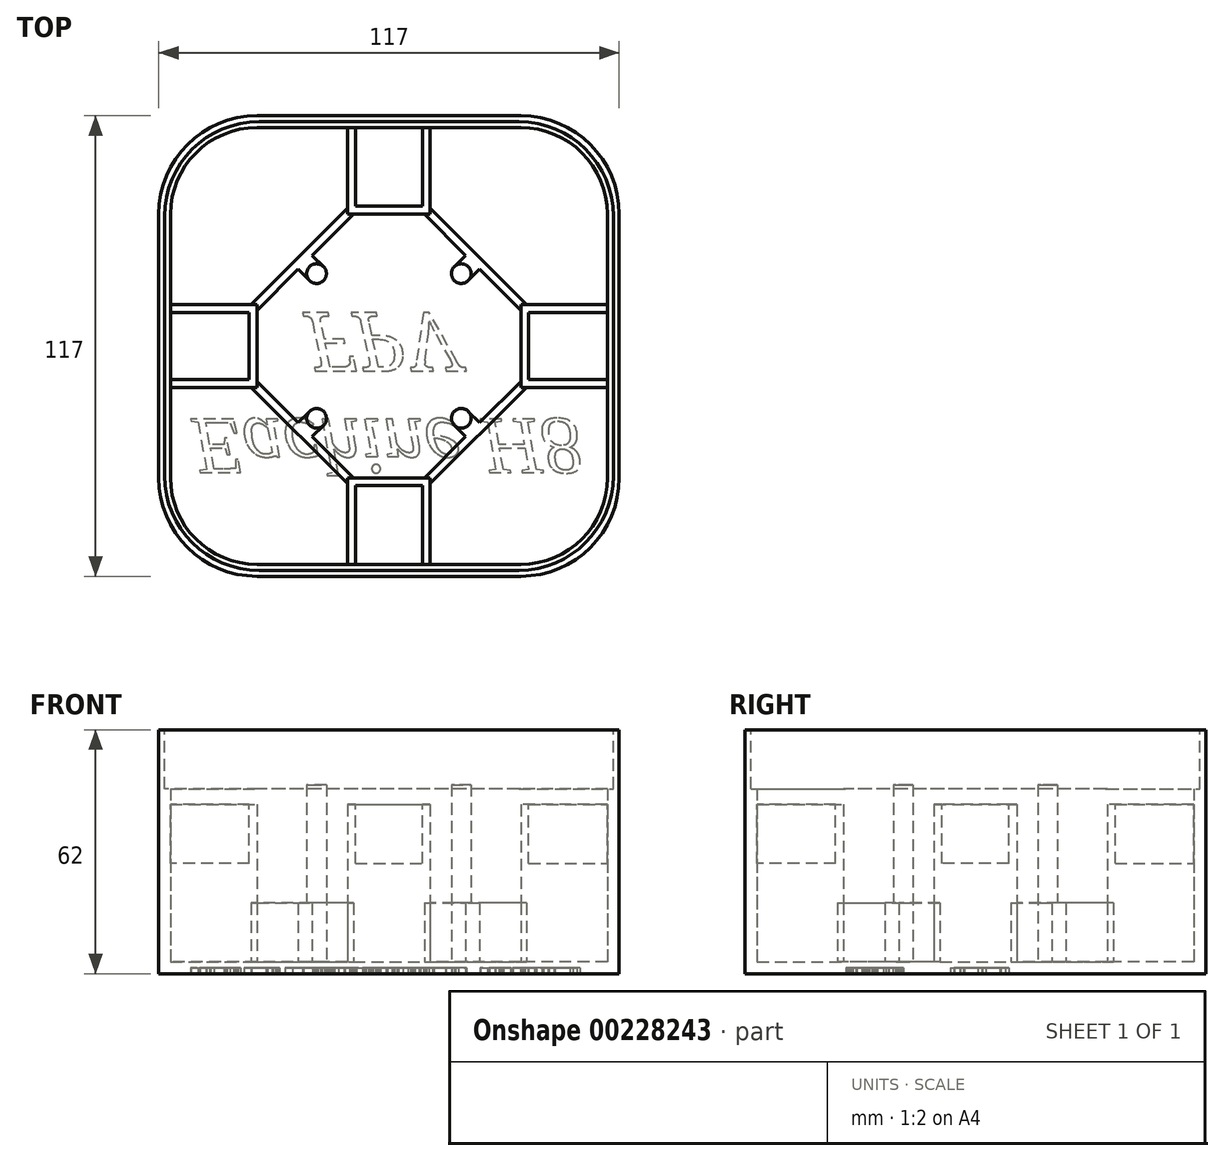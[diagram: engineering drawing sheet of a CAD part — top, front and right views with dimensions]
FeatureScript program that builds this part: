
annotation { "Feature Type Name" : "Feature", "Feature Type Description" : "" }
export const myFeature = defineFeature(function(context is Context, id is Id, definition is map)
    precondition{}
    {
        {
            var Q0;
            Q0=qCreatedBy(makeId("Top.planeOp"),FACE);
            var sketch = newSketch(context, id + "F0", { "sketchPlane" : qUnion([Q0])});
            skLineSegment(sketch, "E0.bottom", {"start": v(33.5, 58.5) * mm, "end": v(-33.5, 58.5) * mm});
            skLineSegment(sketch, "E0.top", {"start": v(33.5, -58.5) * mm, "end": v(-33.5, -58.5) * mm});
            skLineSegment(sketch, "E0.left", {"start": v(58.5, 33.5) * mm, "end": v(58.5, -33.5) * mm});
            skLineSegment(sketch, "E0.right", {"start": v(-58.5, 33.5) * mm, "end": v(-58.5, -33.5) * mm});
            skPoint(sketch, "E0.middle", {"position": v(0, 0) * mm});
            skPoint(sketch, "E1.visualSharp", {"position": v(-58.5, -58.5) * mm});
            skArc(sketch, "E1.filletArc", {"start": v(-58.5, -33.5) * mm, "mid": v(-51.18, -51.18) * mm, "end": v(-33.5, -58.5) * mm});
            skPoint(sketch, "E2.visualSharp", {"position": v(-58.5, 58.5) * mm});
            skArc(sketch, "E2.filletArc", {"start": v(-33.5, 58.5) * mm, "mid": v(-51.18, 51.18) * mm, "end": v(-58.5, 33.5) * mm});
            skPoint(sketch, "E3.visualSharp", {"position": v(58.5, 58.5) * mm});
            skArc(sketch, "E3.filletArc", {"start": v(58.5, 33.5) * mm, "mid": v(51.18, 51.18) * mm, "end": v(33.5, 58.5) * mm});
            skPoint(sketch, "E4.visualSharp", {"position": v(58.5, -58.5) * mm});
            skArc(sketch, "E4.filletArc", {"start": v(33.5, -58.5) * mm, "mid": v(51.18, -51.18) * mm, "end": v(58.5, -33.5) * mm});
            skSolve(sketch);
        }
        {
            var Q0;
            Q0=qSketchRegion(id+"F0",true);
            extrude(context, id + "F1", {"entities" : qUnion([Q0]), "depth" : 62 * mm});
        }
        {
            var Q0;
            Q0=makeQuery(id+"F1.opExtrude","CAP_FACE",FACE,{"disambiguationData":[OSD([sQuery(id+"F0.wireOp",EDGE,"E0.bottom"),sQuery(id+"F0.wireOp",EDGE,"E0.top"),sQuery(id+"F0.wireOp",EDGE,"E0.left"),sQuery(id+"F0.wireOp",EDGE,"E0.right")])],"isStart":false});
            shell(context, id + "F2", {"entities" : qUnion([Q0]), "thickness" : 3 * mm});
        }
        {
            var Q0;
            Q0=makeQuery(id+"F1.opExtrude","CAP_FACE",FACE,{"disambiguationData":[OSD([sQuery(id+"F0.wireOp",EDGE,"E0.bottom"),sQuery(id+"F0.wireOp",EDGE,"E0.top"),sQuery(id+"F0.wireOp",EDGE,"E0.left"),sQuery(id+"F0.wireOp",EDGE,"E0.right")])],"isStart":false});
            var sketch = newSketch(context, id + "F3", { "sketchPlane" : qUnion([Q0])});
            skLineSegment(sketch, "E5.bottom", {"start": v(33, 57) * mm, "end": v(-33, 57) * mm});
            skLineSegment(sketch, "E5.top", {"start": v(33, -57) * mm, "end": v(-33, -57) * mm});
            skLineSegment(sketch, "E5.left", {"start": v(57, 33) * mm, "end": v(57, -33) * mm});
            skLineSegment(sketch, "E5.right", {"start": v(-57, 33) * mm, "end": v(-57, -33) * mm});
            skPoint(sketch, "E5.middle", {"position": v(0, 0) * mm});
            skLineSegment(sketch, "E6.bottom", {"start": v(33.5, 55.5) * mm, "end": v(-33.5, 55.5) * mm});
            skLineSegment(sketch, "E6.top", {"start": v(33.5, -55.5) * mm, "end": v(-33.5, -55.5) * mm});
            skLineSegment(sketch, "E6.left", {"start": v(33.5, 55.5) * mm, "end": v(33.5, -55.5) * mm});
            skLineSegment(sketch, "E6.right", {"start": v(-33.5, 55.5) * mm, "end": v(-33.5, -55.5) * mm});
            skPoint(sketch, "E7.visualSharp", {"position": v(-57, -57) * mm});
            skArc(sketch, "E7.filletArc", {"start": v(-57, -33) * mm, "mid": v(-49.97, -49.97) * mm, "end": v(-33, -57) * mm});
            skPoint(sketch, "E8.visualSharp", {"position": v(57, -57) * mm});
            skArc(sketch, "E8.filletArc", {"start": v(33, -57) * mm, "mid": v(49.97, -49.97) * mm, "end": v(57, -33) * mm});
            skPoint(sketch, "E9.visualSharp", {"position": v(57, 57) * mm});
            skArc(sketch, "E9.filletArc", {"start": v(57, 33) * mm, "mid": v(49.97, 49.97) * mm, "end": v(33, 57) * mm});
            skPoint(sketch, "E10.visualSharp", {"position": v(-57, 57) * mm});
            skArc(sketch, "E10.filletArc", {"start": v(-33, 57) * mm, "mid": v(-49.97, 49.97) * mm, "end": v(-57, 33) * mm});
            skSolve(sketch);
        }
        {
            var Q0;
            Q0=qSketchRegion(id+"F3",true);
            extrude(context, id + "F4", {"entities" : qUnion([Q0]), "operationType" : NewBodyOperationType.REMOVE, "oppositeDirection" : true, "depth" : 15 * mm});
        }
        {
            var Q0;
            Q0=makeQuery(id+"F1.opExtrude","CAP_FACE",FACE,{"disambiguationData":[OSD([sQuery(id+"F0.wireOp",EDGE,"E0.bottom"),sQuery(id+"F0.wireOp",EDGE,"E0.top"),sQuery(id+"F0.wireOp",EDGE,"E0.left"),sQuery(id+"F0.wireOp",EDGE,"E0.right"),sQuery(id+"F0.wireOp",EDGE,"E1.filletArc"),sQuery(id+"F0.wireOp",EDGE,"E2.filletArc"),sQuery(id+"F0.wireOp",EDGE,"E3.filletArc"),sQuery(id+"F0.wireOp",EDGE,"E4.filletArc")])],"isStart":true});
            var sketch = newSketch(context, id + "F5", { "sketchPlane" : qUnion([Q0])});
            skText(sketch, "E11", { "text": "Eachine H8", "fontName": "Tinos-Italic.ttf"});
            skText(sketch, "E12", { "text": "FPV", "fontName": "NotoSerif-Italic.ttf"});
            const initialGuessF5  = {"E11": [-0.05012, 0.0185, 1, 0, 0.015], "E12": [-0.02148, -0.0085, 1, 0, 0.015]};
            skSetInitialGuess(sketch, initialGuessF5);
            skSolve(sketch);
        }
        {
            var Q0;
            Q0=qSketchRegion(id+"F5",true);
            extrude(context, id + "F6", {"entities" : qUnion([Q0]), "operationType" : NewBodyOperationType.REMOVE, "oppositeDirection" : true, "depth" : 1.5 * mm});
        }
        {
            var Q0;
            Q0=makeQuery(id+"F2.opShell","OFFSET_FACE",FACE,{"disambiguationData":[OSD([sQuery(id+"F0.wireOp",EDGE,"E0.bottom"),sQuery(id+"F0.wireOp",EDGE,"E0.top"),sQuery(id+"F0.wireOp",EDGE,"E0.left"),sQuery(id+"F0.wireOp",EDGE,"E0.right"),sQuery(id+"F0.wireOp",EDGE,"E1.filletArc"),sQuery(id+"F0.wireOp",EDGE,"E2.filletArc"),sQuery(id+"F0.wireOp",EDGE,"E3.filletArc"),sQuery(id+"F0.wireOp",EDGE,"E4.filletArc")])]});
            var sketch = newSketch(context, id + "F7", { "sketchPlane" : qUnion([Q0])});
            skLineSegment(sketch, "E13", {"start": v(-18.38, 18.38) * mm, "end": v(18.38, -18.38) * mm, "construction": true});
            skLineSegment(sketch, "E14", {"start": v(-18.38, -18.38) * mm, "end": v(18.38, 18.38) * mm, "construction": true});
            skLineSegment(sketch, "E15.bottom", {"start": v(-18.38, -18.38) * mm, "end": v(18.38, -18.38) * mm, "construction": true});
            skLineSegment(sketch, "E15.top", {"start": v(-18.38, 18.38) * mm, "end": v(18.38, 18.38) * mm, "construction": true});
            skLineSegment(sketch, "E15.left", {"start": v(-18.38, -18.38) * mm, "end": v(-18.38, 18.38) * mm, "construction": true});
            skLineSegment(sketch, "E15.right", {"start": v(18.38, -18.38) * mm, "end": v(18.38, 18.38) * mm, "construction": true});
            skCircle(sketch, "E16", {"center": v(-18.38, 18.38) * mm, "radius": 2.5 * mm});
            skCircle(sketch, "E17", {"center": v(18.38, 18.38) * mm, "radius": 2.5 * mm});
            skCircle(sketch, "E18", {"center": v(18.38, -18.38) * mm, "radius": 2.5 * mm});
            skCircle(sketch, "E19", {"center": v(-18.38, -18.38) * mm, "radius": 2.5 * mm});
            skSolve(sketch);
        }
        {
            var Q0;
            Q0 = qSketchRegion(id + "F7", true);
            extrude(context, id + "F8", {"entities" : qUnion([Q0]), "operationType" : NewBodyOperationType.ADD, "depth" : 45 * mm});
        }
        {
            var Q0;
            Q0=makeQuery(id+"F2.opShell","OFFSET_FACE",FACE,{"disambiguationData":[OSD([sQuery(id+"F0.wireOp",EDGE,"E0.bottom"),sQuery(id+"F0.wireOp",EDGE,"E0.top"),sQuery(id+"F0.wireOp",EDGE,"E0.left"),sQuery(id+"F0.wireOp",EDGE,"E0.right"),sQuery(id+"F0.wireOp",EDGE,"E1.filletArc"),sQuery(id+"F0.wireOp",EDGE,"E2.filletArc"),sQuery(id+"F0.wireOp",EDGE,"E3.filletArc"),sQuery(id+"F0.wireOp",EDGE,"E4.filletArc")])]});
            var sketch = newSketch(context, id + "F9", { "sketchPlane" : qUnion([Q0])});
            skLineSegment(sketch, "E20.bottom", {"start": v(-10.5, 55.5) * mm, "end": v(10.5, 55.5) * mm});
            skLineSegment(sketch, "E20.top", {"start": v(-10.5, 33.5) * mm, "end": v(10.5, 33.5) * mm});
            skLineSegment(sketch, "E20.left", {"start": v(-10.5, 55.5) * mm, "end": v(-10.5, 33.5) * mm});
            skLineSegment(sketch, "E20.right", {"start": v(10.5, 55.5) * mm, "end": v(10.5, 33.5) * mm});
            skLineSegment(sketch, "E21.bottom", {"start": v(55.5, -10.5) * mm, "end": v(33.5, -10.5) * mm});
            skLineSegment(sketch, "E21.top", {"start": v(55.5, 10.5) * mm, "end": v(33.5, 10.5) * mm});
            skLineSegment(sketch, "E21.left", {"start": v(55.5, -10.5) * mm, "end": v(55.5, 10.5) * mm});
            skLineSegment(sketch, "E21.right", {"start": v(33.5, -10.5) * mm, "end": v(33.5, 10.5) * mm});
            skLineSegment(sketch, "E22.bottom", {"start": v(-10.5, -55.5) * mm, "end": v(10.5, -55.5) * mm});
            skLineSegment(sketch, "E22.top", {"start": v(-10.5, -33.5) * mm, "end": v(10.5, -33.5) * mm});
            skLineSegment(sketch, "E22.left", {"start": v(-10.5, -55.5) * mm, "end": v(-10.5, -33.5) * mm});
            skLineSegment(sketch, "E22.right", {"start": v(10.5, -55.5) * mm, "end": v(10.5, -33.5) * mm});
            skLineSegment(sketch, "E23.bottom", {"start": v(-55.5, -10.5) * mm, "end": v(-33.5, -10.5) * mm});
            skLineSegment(sketch, "E23.top", {"start": v(-55.5, 10.5) * mm, "end": v(-33.5, 10.5) * mm});
            skLineSegment(sketch, "E23.left", {"start": v(-55.5, -10.5) * mm, "end": v(-55.5, 10.5) * mm});
            skLineSegment(sketch, "E23.right", {"start": v(-33.5, -10.5) * mm, "end": v(-33.5, 10.5) * mm});
            skSolve(sketch);
        }
        {
            var Q0;
            Q0 = qSketchRegion(id + "F9", true);
            extrude(context, id + "F10", {"entities" : qUnion([Q0]), "operationType" : NewBodyOperationType.ADD, "depth" : 40 * mm});
        }
        {
            var Q0;
            Q0=makeQuery(id+"F10.opExtrude","CAP_FACE",FACE,{"disambiguationData":[OSD([sQuery(id+"F9.wireOp",EDGE,"E23.bottom"),sQuery(id+"F9.wireOp",EDGE,"E23.top"),sQuery(id+"F9.wireOp",EDGE,"E23.left"),sQuery(id+"F9.wireOp",EDGE,"E23.right")])],"isStart":false});
            var sketch = newSketch(context, id + "F11", { "sketchPlane" : qUnion([Q0])});
            skLineSegment(sketch, "E24.bottom", {"start": v(-35.5, 8.5) * mm, "end": v(-55.5, 8.5) * mm});
            skLineSegment(sketch, "E24.top", {"start": v(-35.5, -8.5) * mm, "end": v(-55.5, -8.5) * mm});
            skLineSegment(sketch, "E24.left", {"start": v(-35.5, 8.5) * mm, "end": v(-35.5, -8.5) * mm});
            skLineSegment(sketch, "E24.right", {"start": v(-55.5, 8.5) * mm, "end": v(-55.5, -8.5) * mm});
            skLineSegment(sketch, "E25.bottom", {"start": v(-8.5, 35.5) * mm, "end": v(8.5, 35.5) * mm});
            skLineSegment(sketch, "E25.top", {"start": v(-8.5, 55.5) * mm, "end": v(8.5, 55.5) * mm});
            skLineSegment(sketch, "E25.left", {"start": v(-8.5, 35.5) * mm, "end": v(-8.5, 55.5) * mm});
            skLineSegment(sketch, "E25.right", {"start": v(8.5, 35.5) * mm, "end": v(8.5, 55.5) * mm});
            skLineSegment(sketch, "E26.bottom", {"start": v(35.5, 8.5) * mm, "end": v(55.5, 8.5) * mm});
            skLineSegment(sketch, "E26.top", {"start": v(35.5, -8.5) * mm, "end": v(55.5, -8.5) * mm});
            skLineSegment(sketch, "E26.left", {"start": v(35.5, 8.5) * mm, "end": v(35.5, -8.5) * mm});
            skLineSegment(sketch, "E26.right", {"start": v(55.5, 8.5) * mm, "end": v(55.5, -8.5) * mm});
            skLineSegment(sketch, "E27.bottom", {"start": v(-8.5, -35.5) * mm, "end": v(8.5, -35.5) * mm});
            skLineSegment(sketch, "E27.top", {"start": v(-8.5, -55.5) * mm, "end": v(8.5, -55.5) * mm});
            skLineSegment(sketch, "E27.left", {"start": v(-8.5, -35.5) * mm, "end": v(-8.5, -55.5) * mm});
            skLineSegment(sketch, "E27.right", {"start": v(8.5, -35.5) * mm, "end": v(8.5, -55.5) * mm});
            skSolve(sketch);
        }
        {
            var Q0;
            Q0 = qSketchRegion(id + "F11", true);
            extrude(context, id + "F12", {"entities" : qUnion([Q0]), "operationType" : NewBodyOperationType.REMOVE, "oppositeDirection" : true, "depth" : 15 * mm});
        }
        {
            var Q0;
            Q0=makeQuery(id+"F2.opShell","OFFSET_FACE",FACE,{"disambiguationData":[OSD([sQuery(id+"F0.wireOp",EDGE,"E0.bottom"),sQuery(id+"F0.wireOp",EDGE,"E0.top"),sQuery(id+"F0.wireOp",EDGE,"E0.left"),sQuery(id+"F0.wireOp",EDGE,"E0.right"),sQuery(id+"F0.wireOp",EDGE,"E1.filletArc"),sQuery(id+"F0.wireOp",EDGE,"E2.filletArc"),sQuery(id+"F0.wireOp",EDGE,"E3.filletArc"),sQuery(id+"F0.wireOp",EDGE,"E4.filletArc")])]});
            var sketch = newSketch(context, id + "F13", { "sketchPlane" : qUnion([Q0])});
            skLineSegment(sketch, "E28", {"start": v(-33.5, -10.5) * mm, "end": v(-33.5, -9) * mm});
            skLineSegment(sketch, "E29", {"start": v(-33.5, -9) * mm, "end": v(-9, -33.5) * mm});
            skLineSegment(sketch, "E30", {"start": v(-9, -33.5) * mm, "end": v(-10.5, -33.5) * mm});
            skLineSegment(sketch, "E31", {"start": v(-10.5, -33.5) * mm, "end": v(-10.5, -35) * mm});
            skLineSegment(sketch, "E32", {"start": v(-10.5, -35) * mm, "end": v(-35, -10.5) * mm});
            skLineSegment(sketch, "E33", {"start": v(-35, -10.5) * mm, "end": v(-33.5, -10.5) * mm});
            skLineSegment(sketch, "E34", {"start": v(10.5, -33.5) * mm, "end": v(9, -33.5) * mm});
            skLineSegment(sketch, "E35", {"start": v(9, -33.5) * mm, "end": v(33.5, -9) * mm});
            skLineSegment(sketch, "E36", {"start": v(33.5, -9) * mm, "end": v(33.5, -10.5) * mm});
            skLineSegment(sketch, "E37", {"start": v(33.5, -10.5) * mm, "end": v(35, -10.5) * mm});
            skLineSegment(sketch, "E38", {"start": v(35, -10.5) * mm, "end": v(10.5, -35) * mm});
            skLineSegment(sketch, "E39", {"start": v(10.5, -35) * mm, "end": v(10.5, -33.5) * mm});
            skLineSegment(sketch, "E40", {"start": v(33.5, 10.5) * mm, "end": v(33.5, 9) * mm});
            skLineSegment(sketch, "E41", {"start": v(33.5, 9) * mm, "end": v(9, 33.5) * mm});
            skLineSegment(sketch, "E42", {"start": v(9, 33.5) * mm, "end": v(10.5, 33.5) * mm});
            skLineSegment(sketch, "E43", {"start": v(10.5, 33.5) * mm, "end": v(10.5, 35) * mm});
            skLineSegment(sketch, "E44", {"start": v(10.5, 35) * mm, "end": v(35, 10.5) * mm});
            skLineSegment(sketch, "E45", {"start": v(35, 10.5) * mm, "end": v(33.5, 10.5) * mm});
            skLineSegment(sketch, "E46", {"start": v(-33.5, 10.5) * mm, "end": v(-35, 10.5) * mm});
            skLineSegment(sketch, "E47", {"start": v(-35, 10.5) * mm, "end": v(-10.5, 35) * mm});
            skLineSegment(sketch, "E48", {"start": v(-10.5, 35) * mm, "end": v(-10.5, 33.5) * mm});
            skLineSegment(sketch, "E49", {"start": v(-10.5, 33.5) * mm, "end": v(-9, 33.5) * mm});
            skLineSegment(sketch, "E50", {"start": v(-9, 33.5) * mm, "end": v(-33.5, 9) * mm});
            skLineSegment(sketch, "E51", {"start": v(-33.5, 9) * mm, "end": v(-33.5, 10.5) * mm});
            skSolve(sketch);
        }
        {
            var Q0;
            Q0 = qSketchRegion(id + "F13", true);
            extrude(context, id + "F14", {"entities" : qUnion([Q0]), "operationType" : NewBodyOperationType.ADD, "depth" : 15 * mm});
        }
        {
            var Q0;
            Q0=makeQuery(id+"F14.boolean.opBoolean","SPLIT",FACE,{"disambiguationData":[TD([makeQuery(id+"F8.opExtrude","SWEPT_FACE",FACE,{"disambiguationData":[OSD([sQuery(id+"F7.wireOp",EDGE,"E16")])]})])],"derivedFrom":makeQuery(id+"F2.opShell","OFFSET_FACE",FACE,{"disambiguationData":[OSD([sQuery(id+"F0.wireOp",EDGE,"E0.bottom"),sQuery(id+"F0.wireOp",EDGE,"E0.top"),sQuery(id+"F0.wireOp",EDGE,"E0.left"),sQuery(id+"F0.wireOp",EDGE,"E0.right"),sQuery(id+"F0.wireOp",EDGE,"E1.filletArc"),sQuery(id+"F0.wireOp",EDGE,"E2.filletArc"),sQuery(id+"F0.wireOp",EDGE,"E3.filletArc"),sQuery(id+"F0.wireOp",EDGE,"E4.filletArc")])]})});
            var sketch = newSketch(context, id + "F15", { "sketchPlane" : qUnion([Q0])});
            skLineSegment(sketch, "E52", {"start": v(-19.48, 23.02) * mm, "end": v(-16.62, 20.15) * mm});
            skLineSegment(sketch, "E53", {"start": v(-16.62, 20.15) * mm, "end": v(-20.15, 16.62) * mm});
            skLineSegment(sketch, "E54", {"start": v(-20.15, 16.62) * mm, "end": v(-23.02, 19.48) * mm});
            skLineSegment(sketch, "E55", {"start": v(-23.02, 19.48) * mm, "end": v(-19.48, 23.02) * mm});
            skLineSegment(sketch, "E56", {"start": v(19.48, 23.02) * mm, "end": v(16.62, 20.15) * mm});
            skLineSegment(sketch, "E57", {"start": v(16.62, 20.15) * mm, "end": v(20.15, 16.62) * mm});
            skLineSegment(sketch, "E58", {"start": v(20.15, 16.62) * mm, "end": v(23.02, 19.48) * mm});
            skLineSegment(sketch, "E59", {"start": v(23.02, 19.48) * mm, "end": v(19.48, 23.02) * mm});
            skLineSegment(sketch, "E60", {"start": v(19.48, -23.02) * mm, "end": v(16.62, -20.15) * mm});
            skLineSegment(sketch, "E61", {"start": v(16.62, -20.15) * mm, "end": v(20.15, -16.62) * mm});
            skLineSegment(sketch, "E62", {"start": v(20.15, -16.62) * mm, "end": v(23.02, -19.48) * mm});
            skLineSegment(sketch, "E63", {"start": v(23.02, -19.48) * mm, "end": v(19.48, -23.02) * mm});
            skLineSegment(sketch, "E64", {"start": v(-23.02, -19.48) * mm, "end": v(-20.15, -16.62) * mm});
            skLineSegment(sketch, "E65", {"start": v(-20.15, -16.62) * mm, "end": v(-16.62, -20.15) * mm});
            skLineSegment(sketch, "E66", {"start": v(-16.62, -20.15) * mm, "end": v(-19.48, -23.02) * mm});
            skLineSegment(sketch, "E67", {"start": v(-19.48, -23.02) * mm, "end": v(-23.02, -19.48) * mm});
            skSolve(sketch);
        }
        {
            var Q0;
            Q0 = qSketchRegion(id + "F15", true);
            extrude(context, id + "F16", {"entities" : qUnion([Q0]), "operationType" : NewBodyOperationType.ADD, "depth" : 15 * mm});
        }
    });
